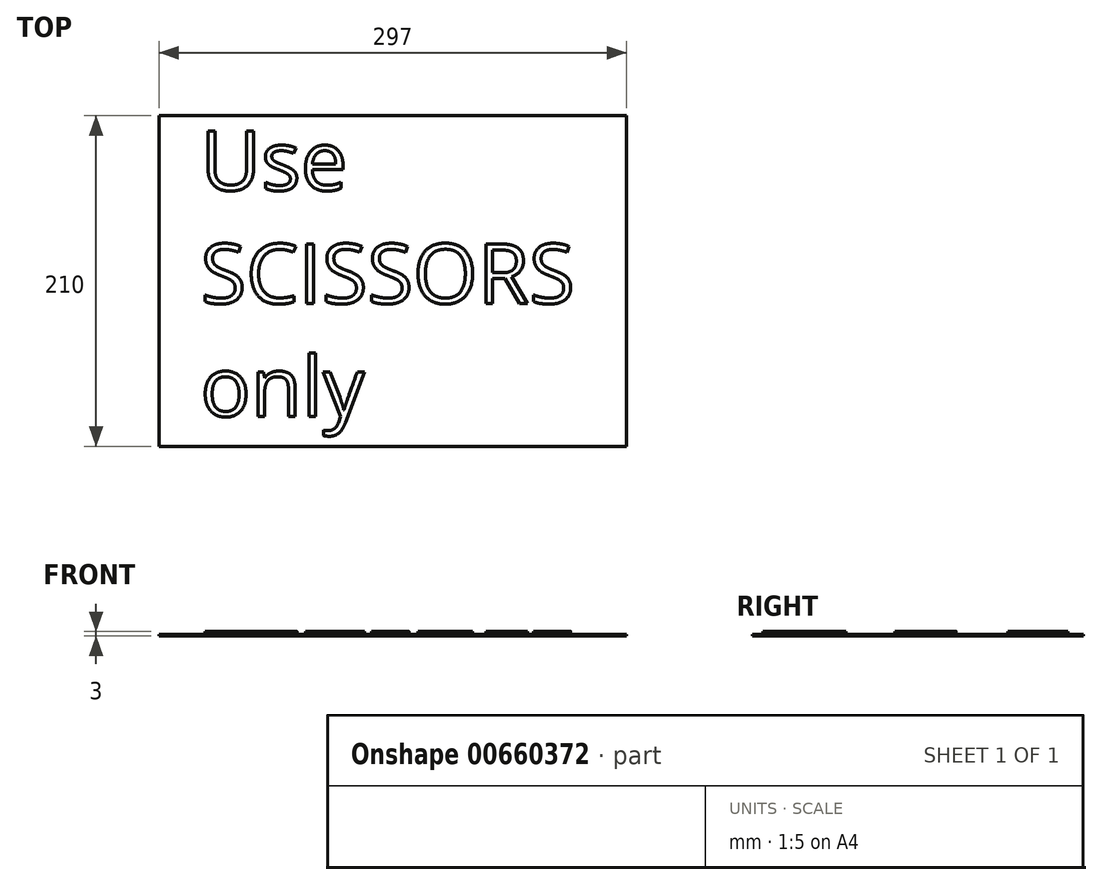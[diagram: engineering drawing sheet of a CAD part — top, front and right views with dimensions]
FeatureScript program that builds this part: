
annotation { "Feature Type Name" : "Feature", "Feature Type Description" : "" }
export const myFeature = defineFeature(function(context is Context, id is Id, definition is map)
    precondition{}
    {
        {
            var Q0;
            Q0=qCreatedBy(makeId("Top.planeOp"),FACE);
            var sketch = newSketch(context, id + "F0", { "sketchPlane" : qUnion([Q0])});
            skLineSegment(sketch, "E0.bottom", {"start": v(-259.32, 190.85) * mm, "end": v(37.68, 190.85) * mm});
            skLineSegment(sketch, "E0.top", {"start": v(-259.32, -19.15) * mm, "end": v(37.68, -19.15) * mm});
            skLineSegment(sketch, "E0.left", {"start": v(-259.32, 190.85) * mm, "end": v(-259.32, -19.15) * mm});
            skLineSegment(sketch, "E0.right", {"start": v(37.68, 190.85) * mm, "end": v(37.68, -19.15) * mm});
            skSolve(sketch);
        }
        {
            var Q0;
            Q0=qSketchRegion(id+"F0",true);
            extrude(context, id + "F1", {"entities" : qUnion([Q0]), "depth" : 1 * mm, "offsetDistance" : 25 * mm});
        }
        {
            var Q0;
            Q0=makeQuery(id+"F1.opExtrude","CAP_FACE",FACE,{"disambiguationData":[OSD([sQuery(id+"F0.wireOp",EDGE,"E0.bottom"),sQuery(id+"F0.wireOp",EDGE,"E0.top"),sQuery(id+"F0.wireOp",EDGE,"E0.left"),sQuery(id+"F0.wireOp",EDGE,"E0.right")])],"isStart":false});
            var sketch = newSketch(context, id + "F2", { "sketchPlane" : qUnion([Q0])});
            skText(sketch, "E1", { "text": "Use\nSCISSORS\nonly", "fontName": "OpenSans-Regular.ttf"});
            const initialGuessF2  = {"E1": [-0.23298, 0.1435, 1, 0, 0.038]};
            skSetInitialGuess(sketch, initialGuessF2);
            skSolve(sketch);
        }
        {
            var Q0;
            Q0=qSketchRegion(id+"F2",true);
            extrude(context, id + "F3", {"entities" : qUnion([Q0]), "operationType" : NewBodyOperationType.ADD, "depth" : 2 * mm, "offsetDistance" : 25 * mm});
        }
    });
